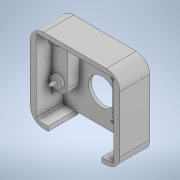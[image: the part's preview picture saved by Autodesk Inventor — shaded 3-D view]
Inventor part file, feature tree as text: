
AUTODESK INVENTOR PART (.ipt)
format: ipt  version: 2022.1 (Build 261234020, 234B)  size: 399,872 bytes
history: mixed  units: in
note: dims shown in document units (in); Inventor stores cm internally (conversion verified against a paired STEP export)
features: sketch x4, extrude x3, hole x1, other x1, imported_body x1
ambient origin geometry x8: Origin, YZ Plane, XZ Plane, XY Plane, X Axis, Y Axis, Z Axis, Center Point
bodies: Solid1 (imported_parasolid)
feature tree (10):
  hole  "Hole1"  [1 undecoded]
  extrude  "Extrusion1"  Depth=0.3937in TaperAngle=0.0deg
  extrude  "Extrusion2"  Depth=0.0394in
  extrude  "Extrusion3"  Depth=0.0787in
  sketch  "Sketch1"  dims[d0=0.3543in d1=0.2362in d2=0.1575in d3=0.0787in d4=90.0deg d5=0.1969in d6=0.8108in d7=0.0394in]
  sketch  "Sketch2"  dims[d8=0.0787in d9=0.3937in d10=0.0in]
  sketch  "Sketch3"  dims[d11=0.0787in d12=0.0394in]
  sketch  "Sketch4"  dims[d13=0.3937in d14=0.0in d15=0.0787in d16=0.0394in d17=0.0787in d18=0.0394in d19=0.3937in d20=0.0in]
  other  "camera_front_box_v003"
  imported_body  NMx_Import_Brep_tag  [imported B-rep: ~53 faces, bbox_mm=[30.0, 28.000001, 10.0]]
note: 1 required parameter value undecoded (feature->parameter linkage not recoverable at this tier; creation-order binding heuristic only, values carry confidence <= 0.55)
